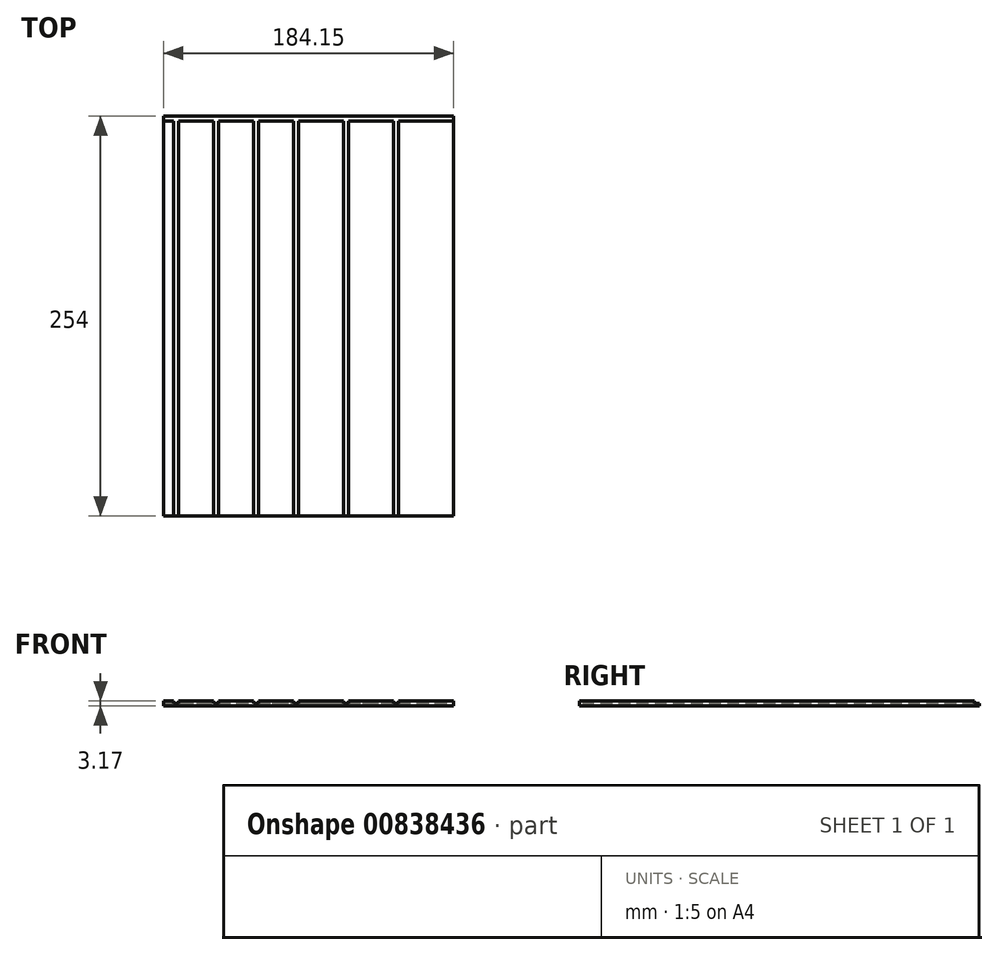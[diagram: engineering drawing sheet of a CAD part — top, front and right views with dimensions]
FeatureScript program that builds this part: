
annotation { "Feature Type Name" : "Feature", "Feature Type Description" : "" }
export const myFeature = defineFeature(function(context is Context, id is Id, definition is map)
    precondition{}
    {
        {
            var Q0;
            Q0=qCreatedBy(makeId("Top.planeOp"),FACE);
            var sketch = newSketch(context, id + "F0", { "sketchPlane" : qUnion([Q0])});
            skLineSegment(sketch, "E0.bottom", {"start": v(0, 0) * mm, "end": v(184.15, 0) * mm});
            skLineSegment(sketch, "E0.top", {"start": v(0, 254) * mm, "end": v(184.15, 254) * mm});
            skLineSegment(sketch, "E0.left", {"start": v(0, 0) * mm, "end": v(0, 254) * mm});
            skLineSegment(sketch, "E0.right", {"start": v(184.15, 0) * mm, "end": v(184.15, 254) * mm});
            skSolve(sketch);
        }
        {
            var Q0;
            Q0=makeQuery(id+"F0.imprint","IMPRINT",FACE,{"disambiguationData":[TD([[makeQuery(id+"F0.imprint","IMPRINT",EDGE,{"derivedFrom":sQuery(id+"F0.wireOp",EDGE,"E0.bottom")}),1.0]])]});
            extrude(context, id + "F1", {"entities" : qUnion([Q0]), "depth" : 3.17 * mm, "offsetDistance" : 25.4 * mm});
        }
        {
            var Q0;
            Q0=makeQuery(id+"F1.opExtrude","CAP_FACE",FACE,{"disambiguationData":[OSD([sQuery(id+"F0.wireOp",EDGE,"E0.bottom"),sQuery(id+"F0.wireOp",EDGE,"E0.top"),sQuery(id+"F0.wireOp",EDGE,"E0.left"),sQuery(id+"F0.wireOp",EDGE,"E0.right")])],"isStart":false});
            var sketch = newSketch(context, id + "F2", { "sketchPlane" : qUnion([Q0])});
            skLineSegment(sketch, "E1.bottom", {"start": v(149.22, 254) * mm, "end": v(146.05, 254) * mm});
            skLineSegment(sketch, "E1.top", {"start": v(149.22, 0) * mm, "end": v(146.05, 0) * mm});
            skLineSegment(sketch, "E1.left", {"start": v(149.22, 254) * mm, "end": v(149.22, 0) * mm});
            skLineSegment(sketch, "E1.right", {"start": v(146.05, 254) * mm, "end": v(146.05, 0) * mm});
            skLineSegment(sketch, "E2.bottom", {"start": v(117.47, 254) * mm, "end": v(114.3, 254) * mm});
            skLineSegment(sketch, "E2.top", {"start": v(117.47, 0) * mm, "end": v(114.3, 0) * mm});
            skLineSegment(sketch, "E2.left", {"start": v(117.47, 254) * mm, "end": v(117.47, 0) * mm});
            skLineSegment(sketch, "E2.right", {"start": v(114.3, 254) * mm, "end": v(114.3, 0) * mm});
            skLineSegment(sketch, "E3.bottom", {"start": v(85.72, 0) * mm, "end": v(82.55, 0) * mm});
            skLineSegment(sketch, "E3.top", {"start": v(85.72, 254) * mm, "end": v(82.55, 254) * mm});
            skLineSegment(sketch, "E3.left", {"start": v(85.72, 0) * mm, "end": v(85.72, 254) * mm});
            skLineSegment(sketch, "E3.right", {"start": v(82.55, 0) * mm, "end": v(82.55, 254) * mm});
            skLineSegment(sketch, "E4.bottom", {"start": v(34.92, 0) * mm, "end": v(31.75, 0) * mm});
            skLineSegment(sketch, "E4.top", {"start": v(34.92, 254) * mm, "end": v(31.75, 254) * mm});
            skLineSegment(sketch, "E4.left", {"start": v(34.92, 0) * mm, "end": v(34.92, 254) * mm});
            skLineSegment(sketch, "E4.right", {"start": v(31.75, 0) * mm, "end": v(31.75, 254) * mm});
            skLineSegment(sketch, "E5.bottom", {"start": v(57.15, 0) * mm, "end": v(60.32, 0) * mm});
            skLineSegment(sketch, "E5.top", {"start": v(57.15, 254) * mm, "end": v(60.32, 254) * mm});
            skLineSegment(sketch, "E5.left", {"start": v(57.15, 0) * mm, "end": v(57.15, 254) * mm});
            skLineSegment(sketch, "E5.right", {"start": v(60.32, 0) * mm, "end": v(60.32, 254) * mm});
            skLineSegment(sketch, "E6.bottom", {"start": v(9.52, 0) * mm, "end": v(6.35, 0) * mm});
            skLineSegment(sketch, "E6.top", {"start": v(9.52, 254) * mm, "end": v(6.35, 254) * mm});
            skLineSegment(sketch, "E6.left", {"start": v(9.52, 0) * mm, "end": v(9.52, 254) * mm});
            skLineSegment(sketch, "E6.right", {"start": v(6.35, 0) * mm, "end": v(6.35, 254) * mm});
            skLineSegment(sketch, "E7", {"start": v(0, 250.83) * mm, "end": v(184.15, 250.83) * mm});
            skSolve(sketch);
        }
        {
            var Q0;
            Q0=makeQuery(id+"F2.imprint","IMPRINT",FACE,{"disambiguationData":[TD([[makeQuery(id+"F2.imprint","IMPRINT",EDGE,{"derivedFrom":sQuery(id+"F2.wireOp",EDGE,"E6.bottom")}),1.0]])]});
            var Q1;
            Q1=makeQuery(id+"F2.imprint","IMPRINT",FACE,{"disambiguationData":[TD([[makeQuery(id+"F2.imprint","IMPRINT",EDGE,{"derivedFrom":sQuery(id+"F2.wireOp",EDGE,"E4.bottom")}),1.0]])]});
            var Q2;
            Q2=makeQuery(id+"F2.imprint","IMPRINT",FACE,{"disambiguationData":[TD([[makeQuery(id+"F2.imprint","IMPRINT",EDGE,{"derivedFrom":sQuery(id+"F2.wireOp",EDGE,"E5.bottom")}),1.0]])]});
            var Q3;
            Q3=makeQuery(id+"F2.imprint","IMPRINT",FACE,{"disambiguationData":[TD([[makeQuery(id+"F2.imprint","IMPRINT",EDGE,{"derivedFrom":sQuery(id+"F2.wireOp",EDGE,"E3.bottom")}),1.0]])]});
            var Q4;
            Q4=makeQuery(id+"F2.imprint","IMPRINT",FACE,{"disambiguationData":[TD([[makeQuery(id+"F2.imprint","IMPRINT",EDGE,{"derivedFrom":sQuery(id+"F2.wireOp",EDGE,"E2.bottom")}),-1.0]])]});
            var Q5;
            Q5=makeQuery(id+"F2.imprint","IMPRINT",FACE,{"disambiguationData":[TD([[makeQuery(id+"F2.imprint","IMPRINT",EDGE,{"derivedFrom":sQuery(id+"F2.wireOp",EDGE,"E1.bottom")}),-1.0]])]});
            var Q6;
            {var subQ0=sQuery(id+"F2.wireOp",EDGE,"E2.top");Q6=makeQuery(id+"F2.imprint","IMPRINT",FACE,{"disambiguationData":[TD([[makeQuery(id+"F2.imprint","IMPRINT",EDGE,{"derivedFrom":subQ0}),1.0]])]});}
            var Q7;
            {var subQ0=sQuery(id+"F2.wireOp",EDGE,"E1.top");Q7=makeQuery(id+"F2.imprint","IMPRINT",FACE,{"disambiguationData":[TD([[makeQuery(id+"F2.imprint","IMPRINT",EDGE,{"derivedFrom":subQ0}),1.0]])]});}
            var Q8;
            {var subQ0=sQuery(id+"F2.wireOp",EDGE,"E3.top");Q8=makeQuery(id+"F2.imprint","IMPRINT",FACE,{"disambiguationData":[TD([[makeQuery(id+"F2.imprint","IMPRINT",EDGE,{"derivedFrom":subQ0}),-1.0]])]});}
            var Q9;
            {var subQ0=sQuery(id+"F2.wireOp",EDGE,"E5.top");Q9=makeQuery(id+"F2.imprint","IMPRINT",FACE,{"disambiguationData":[TD([[makeQuery(id+"F2.imprint","IMPRINT",EDGE,{"derivedFrom":subQ0}),-1.0]])]});}
            var Q10;
            {var subQ0=sQuery(id+"F2.wireOp",EDGE,"E4.top");Q10=makeQuery(id+"F2.imprint","IMPRINT",FACE,{"disambiguationData":[TD([[makeQuery(id+"F2.imprint","IMPRINT",EDGE,{"derivedFrom":subQ0}),-1.0]])]});}
            var Q11;
            {var subQ0=sQuery(id+"F2.wireOp",EDGE,"E6.top");Q11=makeQuery(id+"F2.imprint","IMPRINT",FACE,{"disambiguationData":[TD([[makeQuery(id+"F2.imprint","IMPRINT",EDGE,{"derivedFrom":subQ0}),-1.0]])]});}
            extrude(context, id + "F3", {"entities" : qUnion([Q0, Q1, Q2, Q3, Q4, Q5, Q6, Q7, Q8, Q9, Q10, Q11]), "operationType" : NewBodyOperationType.REMOVE, "oppositeDirection" : true, "depth" : 1.59 * mm, "offsetDistance" : 25.4 * mm});
        }
        {
            var Q0;
            {var subQ3=sQuery(id+"F2.wireOp",EDGE,"E7");var subQ5=makeQuery(id+"F1.opExtrude","CAP_EDGE",EDGE,{"disambiguationData":[OSD([sQuery(id+"F0.wireOp",EDGE,"E0.left")])],"isStart":false});var subQ6=makeQuery(id+"F2.imprint","INTERSECT",VERTEX,{"derivedFrom":[subQ5,subQ3]});Q0=makeQuery(id+"F2.imprint","IMPRINT",FACE,{"disambiguationData":[TD([[makeQuery(id+"F2.imprint","IMPRINT",EDGE,{"disambiguationData":[TD([[subQ6,-1.0]])],"derivedFrom":subQ3}),1.0]])]});}
            var Q1;
            {var subQ0=sQuery(id+"F2.wireOp",EDGE,"E4.right");var subQ3=sQuery(id+"F2.wireOp",EDGE,"E7");var subQ4=makeQuery(id+"F2.imprint","INTERSECT",VERTEX,{"derivedFrom":[subQ0,subQ3]});Q1=makeQuery(id+"F2.imprint","IMPRINT",FACE,{"disambiguationData":[TD([[makeQuery(id+"F2.imprint","IMPRINT",EDGE,{"disambiguationData":[TD([[subQ4,1.0]])],"derivedFrom":subQ3}),1.0]])]});}
            var Q2;
            {var subQ0=sQuery(id+"F2.wireOp",EDGE,"E4.top");Q2=makeQuery(id+"F2.imprint","IMPRINT",FACE,{"disambiguationData":[TD([[makeQuery(id+"F2.imprint","IMPRINT",EDGE,{"derivedFrom":subQ0}),-1.0]])]});}
            var Q3;
            {var subQ0=sQuery(id+"F2.wireOp",EDGE,"E4.left");var subQ3=sQuery(id+"F2.wireOp",EDGE,"E7");var subQ4=makeQuery(id+"F2.imprint","INTERSECT",VERTEX,{"derivedFrom":[subQ0,subQ3]});Q3=makeQuery(id+"F2.imprint","IMPRINT",FACE,{"disambiguationData":[TD([[makeQuery(id+"F2.imprint","IMPRINT",EDGE,{"disambiguationData":[TD([[subQ4,-1.0]])],"derivedFrom":subQ3}),1.0]])]});}
            var Q4;
            {var subQ0=sQuery(id+"F2.wireOp",EDGE,"E6.top");Q4=makeQuery(id+"F2.imprint","IMPRINT",FACE,{"disambiguationData":[TD([[makeQuery(id+"F2.imprint","IMPRINT",EDGE,{"derivedFrom":subQ0}),-1.0]])]});}
            var Q5;
            {var subQ0=sQuery(id+"F2.wireOp",EDGE,"E5.top");Q5=makeQuery(id+"F2.imprint","IMPRINT",FACE,{"disambiguationData":[TD([[makeQuery(id+"F2.imprint","IMPRINT",EDGE,{"derivedFrom":subQ0}),-1.0]])]});}
            var Q6;
            {var subQ0=sQuery(id+"F2.wireOp",EDGE,"E3.right");var subQ3=sQuery(id+"F2.wireOp",EDGE,"E7");var subQ4=makeQuery(id+"F2.imprint","INTERSECT",VERTEX,{"derivedFrom":[subQ0,subQ3]});Q6=makeQuery(id+"F2.imprint","IMPRINT",FACE,{"disambiguationData":[TD([[makeQuery(id+"F2.imprint","IMPRINT",EDGE,{"disambiguationData":[TD([[subQ4,1.0]])],"derivedFrom":subQ3}),1.0]])]});}
            var Q7;
            {var subQ0=sQuery(id+"F2.wireOp",EDGE,"E2.right");var subQ3=sQuery(id+"F2.wireOp",EDGE,"E7");var subQ4=makeQuery(id+"F2.imprint","INTERSECT",VERTEX,{"derivedFrom":[subQ0,subQ3]});Q7=makeQuery(id+"F2.imprint","IMPRINT",FACE,{"disambiguationData":[TD([[makeQuery(id+"F2.imprint","IMPRINT",EDGE,{"disambiguationData":[TD([[subQ4,1.0]])],"derivedFrom":subQ3}),1.0]])]});}
            var Q8;
            {var subQ0=sQuery(id+"F2.wireOp",EDGE,"E3.top");Q8=makeQuery(id+"F2.imprint","IMPRINT",FACE,{"disambiguationData":[TD([[makeQuery(id+"F2.imprint","IMPRINT",EDGE,{"derivedFrom":subQ0}),-1.0]])]});}
            var Q9;
            {var subQ0=sQuery(id+"F2.wireOp",EDGE,"E2.bottom");Q9=makeQuery(id+"F2.imprint","IMPRINT",FACE,{"disambiguationData":[TD([[makeQuery(id+"F2.imprint","IMPRINT",EDGE,{"derivedFrom":subQ0}),-1.0]])]});}
            var Q10;
            {var subQ0=sQuery(id+"F2.wireOp",EDGE,"E1.right");var subQ3=sQuery(id+"F2.wireOp",EDGE,"E7");var subQ4=makeQuery(id+"F2.imprint","INTERSECT",VERTEX,{"derivedFrom":[subQ0,subQ3]});Q10=makeQuery(id+"F2.imprint","IMPRINT",FACE,{"disambiguationData":[TD([[makeQuery(id+"F2.imprint","IMPRINT",EDGE,{"disambiguationData":[TD([[subQ4,1.0]])],"derivedFrom":subQ3}),1.0]])]});}
            var Q11;
            {var subQ0=sQuery(id+"F2.wireOp",EDGE,"E1.bottom");Q11=makeQuery(id+"F2.imprint","IMPRINT",FACE,{"disambiguationData":[TD([[makeQuery(id+"F2.imprint","IMPRINT",EDGE,{"derivedFrom":subQ0}),-1.0]])]});}
            var Q12;
            {var subQ3=sQuery(id+"F2.wireOp",EDGE,"E7");var subQ5=makeQuery(id+"F1.opExtrude","CAP_EDGE",EDGE,{"disambiguationData":[OSD([sQuery(id+"F0.wireOp",EDGE,"E0.right")])],"isStart":false});var subQ7=makeQuery(id+"F2.imprint","INTERSECT",VERTEX,{"derivedFrom":[subQ5,subQ3]});Q12=makeQuery(id+"F2.imprint","IMPRINT",FACE,{"disambiguationData":[TD([[makeQuery(id+"F2.imprint","IMPRINT",EDGE,{"disambiguationData":[TD([[subQ7,1.0]])],"derivedFrom":subQ3}),1.0]])]});}
            extrude(context, id + "F4", {"entities" : qUnion([Q0, Q1, Q2, Q3, Q4, Q5, Q6, Q7, Q8, Q9, Q10, Q11, Q12]), "operationType" : NewBodyOperationType.REMOVE, "oppositeDirection" : true, "depth" : 1.59 * mm, "offsetDistance" : 25.4 * mm});
        }
    });
